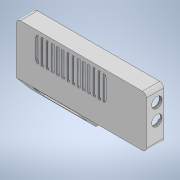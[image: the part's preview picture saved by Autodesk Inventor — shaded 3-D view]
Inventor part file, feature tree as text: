
AUTODESK INVENTOR PART (.ipt)
format: ipt  version: 2021 (Build 250183000, 183)  size: 537,600 bytes
history: native  units: mm
features: sketch x22, extrude x21, chamfer x6, fillet x4, hole x1
ambient origin geometry x8: Origin, YZ Plane, XZ Plane, XY Plane, X Axis, Y Axis, Z Axis, Center Point
bodies: Solid1 (feature_tree)
feature tree (54):
  extrude  "Extrusion1"  Depth=100.0mm
  extrude  "Extrusion3"  Depth=50.0mm
  extrude  "Extrusion4"  Depth=12.5mm
  extrude  "Extrusion12"  Depth=3.0mm TaperAngle=0.0deg
  extrude  "Extrusion13"  Depth=3.0mm TaperAngle=0.0deg
  fillet  "Fillet3"  Radius=2.0mm
  extrude  "Extrusion15"  Depth=2.0mm
  extrude  "Extrusion20"  Depth=1.2mm
  extrude  "Extrusion21"  Depth=12.0mm TaperAngle=0.0deg
  extrude  "Extrusion22"  Depth=2.0mm
  extrude  "Extrusion23"  Depth=3.0mm
  extrude  "Extrusion26"  Depth=4.4mm TaperAngle=0.0deg
  hole  "Hole2"  [1 undecoded]
  chamfer  "Chamfer3"  Distance=12.0mm
  chamfer  "Chamfer4"  Distance=12.0mm
  chamfer  "Chamfer5"  Distance=2.0mm
  chamfer  "Chamfer6"  Distance=2.0mm
  chamfer  "Chamfer7"  Distance=3.0mm
  extrude  "Extrusion27"  Depth=3.0mm
  fillet  "Fillet4"  Radius=3.0mm
  extrude  "Extrusion28"  Depth=50.0mm
  extrude  "Extrusion29"  Depth=0.5mm
  extrude  "Extrusion30"  Depth=15.0mm
  fillet  "Fillet5"  Radius=3.0mm
  extrude  "Extrusion34"  Depth=3.0mm
  extrude  "Extrusion35"  Depth=0.5mm
  extrude  "Extrusion36"  Depth=0.5mm
  extrude  "Extrusion37"  Depth=0.5mm
  fillet  "Fillet6"  Radius=4.8mm
  extrude  "Extrusion38"  Depth=0.5mm
  extrude  "Extrusion39"  Depth=0.5mm
  chamfer  "Chamfer8"  Distance=4.8mm
  sketch  "Sketch1"  dims[d0=52.0mm d1=100.0mm]
  sketch  "Sketch4"  dims[d2=26.0mm d3=50.0mm]
  sketch  "Sketch5"  dims[d4=1.2mm d5=0.0mm d35=12.5mm]
  sketch  "Sketch13"  dims[d36=63.1mm d37=3.0mm d38=0.0mm]
  sketch  "Sketch14"  dims[d39=50.673mm d40=3.0mm d41=0.0mm d79=2.0mm]
  sketch  "Sketch16"  dims[d80=2.0mm d81=2.0mm]
  sketch  "Sketch21"  dims[d82=1.2mm d83=44.0mm]
  sketch  "Sketch22"  dims[d84=59.0mm d85=12.0mm d86=0.0mm]
  sketch  "Sketch23"  dims[d87=2.0mm d88=12.6mm]
  sketch  "Sketch24"  dims[d89=12.0mm d90=0.0mm d91=3.0mm]
  sketch  "Sketch27"  dims[d95=33.8mm d96=4.4mm d97=0.0mm]
  sketch  "Sketch28"  dims[d117=2.0mm d118=2.0mm d119=12.0mm d120=0.0mm d121=12.0mm d122=0.0mm]
  sketch  "Sketch29"  dims[d123=70.0mm]
  sketch  "Sketch30"  dims[d124=89.0mm]
  sketch  "Sketch31"  dims[d125=8.0mm]
  sketch  "Sketch32"  dims[d126=8.0mm d127=2.0mm d128=0.0mm]
  sketch  "Sketch36"  dims[d129=8.0mm]
  sketch  "Sketch37"  dims[d130=10.0mm]
  sketch  "Sketch38"  dims[d131=12.0mm]
  sketch  "Sketch39"  dims[d132=8.0mm]
  sketch  "Sketch40"  dims[d133=8.0mm]
  sketch  "Sketch41"  dims[d134=8.0mm d135=2.0mm d136=0.0mm d144=3.0mm d145=3.0mm d146=3.0mm d147=50.0mm d148=97.0mm d149=15.0mm d150=3.0mm d151=3.0mm d152=97.0mm d153=49.0mm d154=4.8mm d155=4.8mm d156=4.8mm d157=4.8mm d158=4.8mm d159=5.0mm d160=0.0mm d161=2.0mm d162=6.0mm d163=4.0mm d164=2.0mm d165=90.0deg d166=4.0mm d167=20.594885mm d168=2.0mm d169=2.0mm d170=45.0deg d171=1.0mm d172=2.0mm d173=45.0deg d174=2.0mm d175=2.0mm d176=45.0deg d177=2.0mm d178=2.0mm d179=45.0deg d180=0.8mm d181=2.0mm d182=45.0deg d184=68.0mm d189=2.0mm d190=0.0mm d191=2.0mm d192=2.0mm d193=24.0mm d194=2.0mm d195=0.0mm d196=36.5mm d197=46.5mm d198=3.5mm d199=2.0mm d200=0.0mm d201=12.5mm d202=23.0mm d203=3.5mm d204=2.0mm d205=0.0mm d206=1.0mm d217=7.6mm d218=10.0mm d219=46.4mm d220=20.0mm d221=0.0mm d222=22.68928mm d223=67.0mm d224=0.0mm d225=1.2mm d226=0.0mm d227=1.2mm d228=0.0mm d229=3.0mm d230=12.3mm d231=33.2mm d232=1.0mm d233=10.0mm d234=1.2mm d235=0.0mm d236=1.2mm d237=5.0mm d238=20.0mm d239=1.5mm d240=0.0mm d241=1.5mm d242=2.0mm d243=45.0deg d67=0.5mm d68=0.872665mm d69=0.5mm d70=0.872665mm d71=0.5mm d72=0.872665mm d73=0.5mm d74=0.872665mm d75=0.872665mm d76=0.5mm d77=0.872665mm d208=0.5mm d209=0.872665mm d210=0.5mm d211=0.872665mm]
note: 1 required parameter value undecoded (feature->parameter linkage not recoverable at this tier; creation-order binding heuristic only, values carry confidence <= 0.55)
